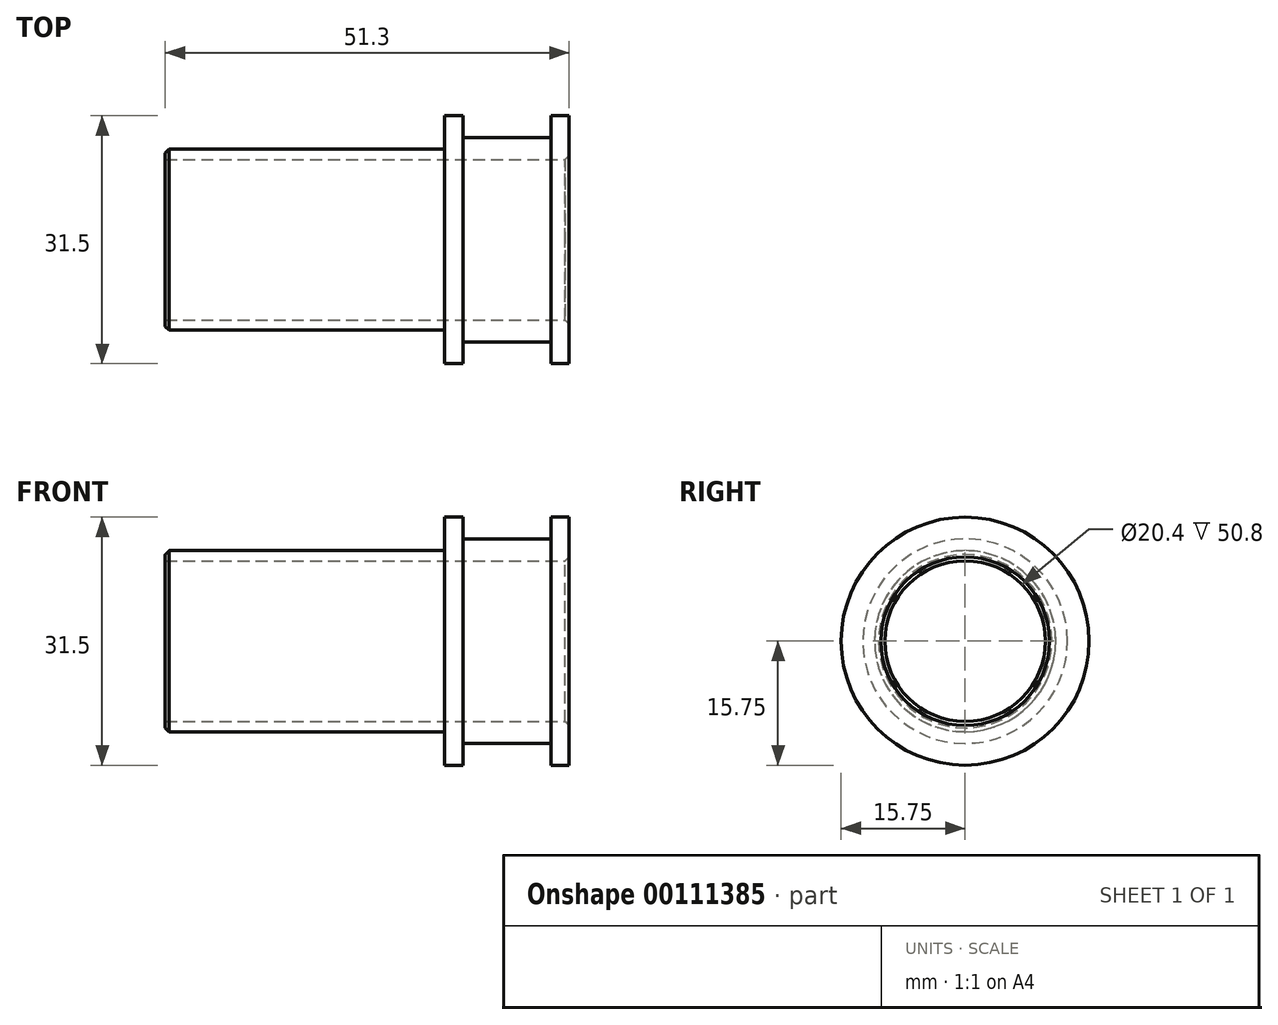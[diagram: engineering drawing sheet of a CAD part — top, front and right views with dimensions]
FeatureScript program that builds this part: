
annotation { "Feature Type Name" : "Feature", "Feature Type Description" : "" }
export const myFeature = defineFeature(function(context is Context, id is Id, definition is map)
    precondition{}
    {
        {
            var Q0;
            Q0=qCreatedBy(makeId("Top.planeOp"),FACE);
            var sketch = newSketch(context, id + "F0", { "sketchPlane" : qUnion([Q0])});
            skLineSegment(sketch, "E0", {"start": v(-51.3, 10.2) * mm, "end": v(0, 10.2) * mm});
            skLineSegment(sketch, "E1", {"start": v(0, 10.2) * mm, "end": v(0, 15.75) * mm});
            skLineSegment(sketch, "E2", {"start": v(0, 15.75) * mm, "end": v(-2.3, 15.75) * mm});
            skLineSegment(sketch, "E3", {"start": v(-2.3, 15.75) * mm, "end": v(-2.3, 13) * mm});
            skLineSegment(sketch, "E4", {"start": v(-2.3, 13) * mm, "end": v(-13.5, 13) * mm});
            skLineSegment(sketch, "E5", {"start": v(-13.5, 13) * mm, "end": v(-13.5, 15.75) * mm});
            skLineSegment(sketch, "E6", {"start": v(-13.5, 15.75) * mm, "end": v(-15.8, 15.75) * mm});
            skLineSegment(sketch, "E7", {"start": v(-15.8, 15.75) * mm, "end": v(-15.8, 11.5) * mm});
            skLineSegment(sketch, "E8", {"start": v(-15.8, 11.5) * mm, "end": v(-51.3, 11.5) * mm});
            skLineSegment(sketch, "E9", {"start": v(-51.3, 11.5) * mm, "end": v(-51.3, 10.2) * mm});
            skLineSegment(sketch, "E10", {"start": v(0, 0) * mm, "end": v(-55.88, 0) * mm, "construction": true});
            skSolve(sketch);
        }
        {
            var Q0;
            Q0=makeQuery(id+"F0.imprint","IMPRINT",FACE,{"disambiguationData":[TD([[makeQuery(id+"F0.imprint","IMPRINT",EDGE,{"derivedFrom":sQuery(id+"F0.wireOp",EDGE,"E0")}),1.0]])]});
            var Q1;
            Q1=sQuery(id+"F0.wireOp",EDGE,"E7");
            var Q2;
            Q2=sQuery(id+"F0.wireOp",EDGE,"E9");
            var Q3;
            Q3=sQuery(id+"F0.wireOp",EDGE,"E8");
            var Q4;
            Q4=sQuery(id+"F0.wireOp",EDGE,"E5");
            var Q5;
            Q5=sQuery(id+"F0.wireOp",EDGE,"E6");
            var Q6;
            Q6=sQuery(id+"F0.wireOp",EDGE,"E4");
            var Q7;
            Q7=sQuery(id+"F0.wireOp",EDGE,"E1");
            var Q8;
            Q8=sQuery(id+"F0.wireOp",EDGE,"E3");
            var Q9;
            Q9=sQuery(id+"F0.wireOp",EDGE,"E2");
            var Q10;
            Q10=sQuery(id+"F0.wireOp",EDGE,"E0");
            var Q11;
            Q11=sQuery(id+"F0.wireOp",EDGE,"E10");
            revolve(context, id + "F1", {"entities" : qUnion([Q0]), "surfaceEntities" : qUnion([Q1, Q2, Q3, Q4, Q5, Q6, Q7, Q8, Q9, Q10]), "axis" : qUnion([Q11]), "revolveType" : RevolveType.FULL});
        }
        {
            var Q0;
            Q0=makeQuery(id+"F1.opRevolve","SWEPT_EDGE",EDGE,{"disambiguationData":[OSD([sQuery(id+"F0.wireOp",EDGE,"E8"),sQuery(id+"F0.wireOp",EDGE,"E9")])]});
            var Q1;
            Q1=makeQuery(id+"F1.opRevolve","SWEPT_EDGE",EDGE,{"disambiguationData":[OSD([sQuery(id+"F0.wireOp",EDGE,"E0"),sQuery(id+"F0.wireOp",EDGE,"E1")])]});
            chamfer(context, id + "F2", {"entities" : qUnion([Q0, Q1]), "width" : 0.5 * mm, "tangentPropagation" : true});
        }
    });
